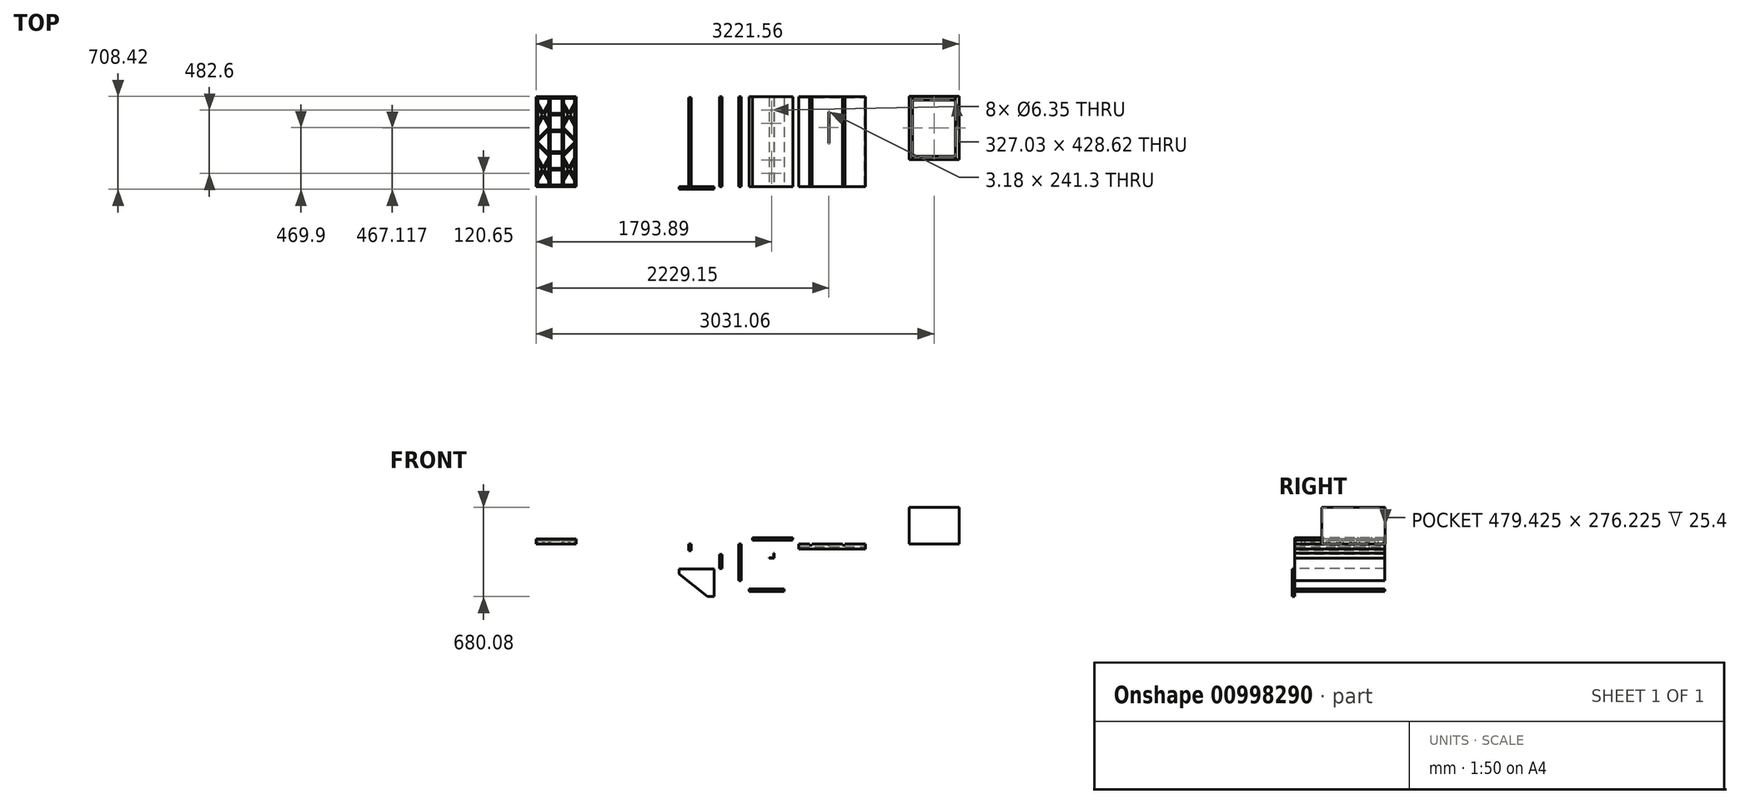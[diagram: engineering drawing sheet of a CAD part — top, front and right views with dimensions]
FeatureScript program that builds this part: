
annotation { "Feature Type Name" : "Feature", "Feature Type Description" : "" }
export const myFeature = defineFeature(function(context is Context, id is Id, definition is map)
    precondition{}
    {
        {
            var Q0;
            Q0=qCreatedBy(makeId("Front.planeOp"),FACE);
            var sketch = newSketch(context, id + "F0", { "sketchPlane" : qUnion([Q0])});
            skLineSegment(sketch, "E0", {"start": v(0, 0) * mm, "end": v(508, 0) * mm});
            skLineSegment(sketch, "E1", {"start": v(508, 0) * mm, "end": v(508, -38.1) * mm});
            skLineSegment(sketch, "E2", {"start": v(508, -38.1) * mm, "end": v(0, -38.1) * mm});
            skLineSegment(sketch, "E3", {"start": v(0, -38.1) * mm, "end": v(0, 0) * mm});
            skSolve(sketch);
        }
        {
            var Q0;
            Q0=makeQuery(id+"F0.imprint","IMPRINT",FACE,{"disambiguationData":[TD([[makeQuery(id+"F0.imprint","IMPRINT",EDGE,{"derivedFrom":sQuery(id+"F0.wireOp",EDGE,"E0")}),-1.0]])]});
            extrude(context, id + "F1", {"entities" : qUnion([Q0]), "oppositeDirection" : true, "depth" : 685.8 * mm, "offsetDistance" : 25.4 * mm});
        }
        {
            var Q0;
            Q0=qCreatedBy(makeId("Front.planeOp"),FACE);
            var sketch = newSketch(context, id + "F2", { "sketchPlane" : qUnion([Q0])});
            skLineSegment(sketch, "E4", {"start": v(-187.6, -68.5) * mm, "end": v(-187.6, -106.6) * mm});
            skLineSegment(sketch, "E5", {"start": v(-187.6, -106.6) * mm, "end": v(-225.7, -106.6) * mm});
            skLineSegment(sketch, "E6", {"start": v(-225.7, -106.6) * mm, "end": v(-225.7, -103.42) * mm});
            skLineSegment(sketch, "E7", {"start": v(-225.7, -103.42) * mm, "end": v(-190.78, -103.42) * mm});
            skLineSegment(sketch, "E8", {"start": v(-190.78, -103.42) * mm, "end": v(-190.78, -68.5) * mm});
            skLineSegment(sketch, "E9", {"start": v(-190.78, -68.5) * mm, "end": v(-187.6, -68.5) * mm});
            skSolve(sketch);
        }
        {
            var Q0;
            Q0=makeQuery(id+"F2.imprint","IMPRINT",FACE,{"disambiguationData":[TD([[makeQuery(id+"F2.imprint","IMPRINT",EDGE,{"derivedFrom":sQuery(id+"F2.wireOp",EDGE,"E4")}),-1.0]])]});
            var Q1;
            Q1=makeQuery(id+"F1.opExtrude","CAP_VERTEX",VERTEX,{"disambiguationData":[OSD([sQuery(id+"F0.wireOp",EDGE,"E0"),sQuery(id+"F0.wireOp",EDGE,"E3")])],"isStart":false});
            extrude(context, id + "F3", {"entities" : qUnion([Q0]), "endBound" : BoundingType.UP_TO_VERTEX, "oppositeDirection" : true, "depth" : 25.4 * mm, "endBoundEntityVertex" : qUnion([Q1]), "offsetDistance" : 25.4 * mm});
        }
        {
            var Q0;
            Q0=qCreatedBy(makeId("Front.planeOp"),FACE);
            var sketch = newSketch(context, id + "F4", { "sketchPlane" : qUnion([Q0])});
            skLineSegment(sketch, "E10.bottom", {"start": v(-351.49, 47.66) * mm, "end": v(-46.69, 47.66) * mm});
            skLineSegment(sketch, "E10.top", {"start": v(-351.49, 28.61) * mm, "end": v(-46.69, 28.61) * mm});
            skLineSegment(sketch, "E10.left", {"start": v(-351.49, 47.66) * mm, "end": v(-351.49, 28.61) * mm});
            skLineSegment(sketch, "E10.right", {"start": v(-46.69, 47.66) * mm, "end": v(-46.69, 28.61) * mm});
            skSolve(sketch);
        }
        {
            var Q0;
            Q0=makeQuery(id+"F4.imprint","IMPRINT",FACE,{"disambiguationData":[TD([[makeQuery(id+"F4.imprint","IMPRINT",EDGE,{"derivedFrom":sQuery(id+"F4.wireOp",EDGE,"E10.bottom")}),-1.0]])]});
            var Q1;
            Q1=makeQuery(id+"F1.opExtrude","CAP_VERTEX",VERTEX,{"disambiguationData":[OSD([sQuery(id+"F0.wireOp",EDGE,"E0"),sQuery(id+"F0.wireOp",EDGE,"E3")])],"isStart":false});
            extrude(context, id + "F5", {"entities" : qUnion([Q0]), "endBound" : BoundingType.UP_TO_VERTEX, "oppositeDirection" : true, "depth" : 25.4 * mm, "endBoundEntityVertex" : qUnion([Q1]), "offsetDistance" : 25.4 * mm});
        }
        {
            var Q0;
            Q0=qCreatedBy(makeId("Front.planeOp"),FACE);
            var sketch = newSketch(context, id + "F6", { "sketchPlane" : qUnion([Q0])});
            skLineSegment(sketch, "E11", {"start": v(-457.67, 0) * mm, "end": v(-438.62, 0) * mm});
            skLineSegment(sketch, "E12", {"start": v(-438.62, -279.4) * mm, "end": v(-457.67, -279.4) * mm});
            skLineSegment(sketch, "E13", {"start": v(-457.67, -279.4) * mm, "end": v(-457.67, 0) * mm});
            skLineSegment(sketch, "E14", {"start": v(-438.62, -279.4) * mm, "end": v(-438.62, 0) * mm});
            skSolve(sketch);
        }
        {
            var Q0;
            Q0=makeQuery(id+"F6.imprint","IMPRINT",FACE,{"disambiguationData":[TD([[makeQuery(id+"F6.imprint","IMPRINT",EDGE,{"derivedFrom":sQuery(id+"F6.wireOp",EDGE,"E11")}),-1.0]])]});
            var Q1;
            Q1=makeQuery(id+"F1.opExtrude","CAP_VERTEX",VERTEX,{"disambiguationData":[OSD([sQuery(id+"F0.wireOp",EDGE,"E0"),sQuery(id+"F0.wireOp",EDGE,"E3")])],"isStart":false});
            extrude(context, id + "F7", {"entities" : qUnion([Q0]), "operationType" : NewBodyOperationType.ADD, "endBound" : BoundingType.UP_TO_VERTEX, "oppositeDirection" : true, "depth" : 25.4 * mm, "endBoundEntityVertex" : qUnion([Q1]), "offsetDistance" : 25.4 * mm});
        }
        {
            var Q0;
            Q0=makeQuery(id+"F1.opExtrude","SWEPT_FACE",FACE,{"disambiguationData":[OSD([sQuery(id+"F0.wireOp",EDGE,"E2")])]});
            var sketch = newSketch(context, id + "F8", { "sketchPlane" : qUnion([Q0])});
            skLineSegment(sketch, "E15.bottom", {"start": v(6.35, -6.35) * mm, "end": v(501.65, -6.35) * mm});
            skLineSegment(sketch, "E15.top", {"start": v(6.35, -679.45) * mm, "end": v(501.65, -679.45) * mm});
            skLineSegment(sketch, "E15.left", {"start": v(6.35, -6.35) * mm, "end": v(6.35, -679.45) * mm});
            skLineSegment(sketch, "E15.right", {"start": v(501.65, -6.35) * mm, "end": v(501.65, -679.45) * mm});
            skSolve(sketch);
        }
        {
            var Q0;
            Q0=makeQuery(id+"F8.imprint","IMPRINT",FACE,{"disambiguationData":[TD([[makeQuery(id+"F8.imprint","IMPRINT",EDGE,{"derivedFrom":sQuery(id+"F8.wireOp",EDGE,"E15.bottom")}),-1.0]])]});
            extrude(context, id + "F9", {"entities" : qUnion([Q0]), "operationType" : NewBodyOperationType.REMOVE, "oppositeDirection" : true, "depth" : 19.05 * mm, "offsetDistance" : 25.4 * mm});
        }
        {
            var Q0;
            Q0=makeQuery(id+"F5.opExtrude","SWEPT_FACE",FACE,{"disambiguationData":[OSD([sQuery(id+"F4.wireOp",EDGE,"E10.right")])]});
            var sketch = newSketch(context, id + "F10", { "sketchPlane" : qUnion([Q0])});
            skLineSegment(sketch, "E16", {"start": v(0, 41.31) * mm, "end": v(685.8, 41.31) * mm});
            skSolve(sketch);
        }
        {
            var Q0;
            {var subQ0=sQuery(id+"F10.wireOp",EDGE,"E16");Q0=makeQuery(id+"F10.imprint","IMPRINT",FACE,{"disambiguationData":[TD([[makeQuery(id+"F10.imprint","IMPRINT",EDGE,{"derivedFrom":subQ0}),1.0]])]});}
            extrude(context, id + "F11", {"entities" : qUnion([Q0]), "operationType" : NewBodyOperationType.ADD, "depth" : 3.17 * mm, "offsetDistance" : 25.4 * mm});
        }
        {
            var Q0;
            Q0=makeQuery(id+"F3.opExtrude","SWEPT_FACE",FACE,{"disambiguationData":[OSD([sQuery(id+"F2.wireOp",EDGE,"E5")])]});
            var sketch = newSketch(context, id + "F12", { "sketchPlane" : qUnion([Q0])});
            skCircle(sketch, "E17", {"center": v(-206.66, -101.6) * mm, "radius": 3.18 * mm});
            skPoint(sketch, "E17.centerSnap0", {"position": v(-206.66, 0) * mm});
            skCircle(sketch, "E18", {"center": v(-206.66, -203.2) * mm, "radius": 3.18 * mm});
            skCircle(sketch, "E19", {"center": v(-206.66, -482.6) * mm, "radius": 3.18 * mm});
            skCircle(sketch, "E20", {"center": v(-206.66, -584.2) * mm, "radius": 3.18 * mm});
            skLineSegment(sketch, "E21", {"start": v(-206.66, 0) * mm, "end": v(-206.66, -685.8) * mm, "construction": true});
            skSolve(sketch);
        }
        {
            var Q0;
            Q0 = qSketchRegion(id + "F12", true);
            extrude(context, id + "F13", {"entities" : qUnion([Q0]), "operationType" : NewBodyOperationType.REMOVE, "endBound" : BoundingType.THROUGH_ALL, "oppositeDirection" : true, "depth" : 25.4 * mm, "offsetDistance" : 25.4 * mm});
        }
        {
            var Q0;
            Q0=qCreatedBy(makeId("Front.planeOp"),FACE);
            var sketch = newSketch(context, id + "F14", { "sketchPlane" : qUnion([Q0])});
            skLineSegment(sketch, "E22.bottom", {"start": v(-377.25, -343.66) * mm, "end": v(-110.55, -343.66) * mm});
            skLineSegment(sketch, "E22.top", {"start": v(-377.25, -362.7) * mm, "end": v(-110.55, -362.7) * mm});
            skLineSegment(sketch, "E22.left", {"start": v(-377.25, -343.66) * mm, "end": v(-377.25, -362.7) * mm});
            skLineSegment(sketch, "E22.right", {"start": v(-110.55, -343.66) * mm, "end": v(-110.55, -362.7) * mm});
            skSolve(sketch);
        }
        {
            var Q0;
            Q0 = qSketchRegion(id + "F14", true);
            var Q1;
            Q1=makeQuery(id+"F1.opExtrude","CAP_VERTEX",VERTEX,{"disambiguationData":[OSD([sQuery(id+"F0.wireOp",EDGE,"E0"),sQuery(id+"F0.wireOp",EDGE,"E3")])],"isStart":false});
            extrude(context, id + "F15", {"entities" : qUnion([Q0]), "endBound" : BoundingType.UP_TO_VERTEX, "oppositeDirection" : true, "depth" : 25.4 * mm, "endBoundEntityVertex" : qUnion([Q1]), "offsetDistance" : 25.4 * mm});
        }
        {
            var Q0;
            Q0=qCreatedBy(makeId("Front.planeOp"),FACE);
            var sketch = newSketch(context, id + "F16", { "sketchPlane" : qUnion([Q0])});
            skLineSegment(sketch, "E23.bottom", {"start": v(-839.36, 0) * mm, "end": v(-820.3, 0) * mm});
            skLineSegment(sketch, "E23.top", {"start": v(-839.36, -50.8) * mm, "end": v(-820.3, -50.8) * mm});
            skLineSegment(sketch, "E23.left", {"start": v(-839.36, 0) * mm, "end": v(-839.36, -50.8) * mm});
            skLineSegment(sketch, "E23.right", {"start": v(-820.3, 0) * mm, "end": v(-820.3, -50.8) * mm});
            skSolve(sketch);
        }
        {
            var Q0;
            Q0 = qSketchRegion(id + "F16", true);
            var Q1;
            Q1=makeQuery(id+"F9.boolean.opBoolean","COPY",VERTEX,{"derivedFrom":makeQuery(id+"F9.opExtrude","CAP_VERTEX",VERTEX,{"disambiguationData":[OSD([sQuery(id+"F8.wireOp",EDGE,"E15.top"),sQuery(id+"F8.wireOp",EDGE,"E15.left")])],"isStart":false})});
            extrude(context, id + "F17", {"entities" : qUnion([Q0]), "endBound" : BoundingType.UP_TO_VERTEX, "oppositeDirection" : true, "depth" : 25.4 * mm, "endBoundEntityVertex" : qUnion([Q1]), "offsetDistance" : 25.4 * mm});
        }
        {
            var Q0;
            Q0=qCreatedBy(makeId("Front.planeOp"),FACE);
            var sketch = newSketch(context, id + "F18", { "sketchPlane" : qUnion([Q0])});
            skLineSegment(sketch, "E24.bottom", {"start": v(-602.45, -79.5) * mm, "end": v(-583.4, -79.5) * mm});
            skLineSegment(sketch, "E24.top", {"start": v(-602.45, -187.44) * mm, "end": v(-583.4, -187.44) * mm});
            skLineSegment(sketch, "E24.left", {"start": v(-602.45, -79.5) * mm, "end": v(-602.45, -187.44) * mm});
            skLineSegment(sketch, "E24.right", {"start": v(-583.4, -79.5) * mm, "end": v(-583.4, -187.44) * mm});
            skSolve(sketch);
        }
        {
            var Q0;
            Q0 = qSketchRegion(id + "F18", true);
            var Q1;
            Q1=makeQuery(id+"F1.opExtrude","CAP_VERTEX",VERTEX,{"disambiguationData":[OSD([sQuery(id+"F0.wireOp",EDGE,"E0"),sQuery(id+"F0.wireOp",EDGE,"E3")])],"isStart":false});
            extrude(context, id + "F19", {"entities" : qUnion([Q0]), "endBound" : BoundingType.UP_TO_VERTEX, "oppositeDirection" : true, "depth" : 25.4 * mm, "endBoundEntityVertex" : qUnion([Q1]), "offsetDistance" : 25.4 * mm});
        }
        {
            var Q0;
            Q0=qCreatedBy(makeId("Front.planeOp"),FACE);
            var sketch = newSketch(context, id + "F20", { "sketchPlane" : qUnion([Q0])});
            skLineSegment(sketch, "E25", {"start": v(-912.68, -191.13) * mm, "end": v(-645.98, -191.13) * mm});
            skLineSegment(sketch, "E26", {"start": v(-645.98, -191.13) * mm, "end": v(-645.98, -400.68) * mm});
            skLineSegment(sketch, "E27", {"start": v(-912.68, -191.13) * mm, "end": v(-912.68, -229.23) * mm});
            skLineSegment(sketch, "E28", {"start": v(-645.98, -400.68) * mm, "end": v(-696.78, -400.68) * mm});
            skLineSegment(sketch, "E29", {"start": v(-696.78, -400.68) * mm, "end": v(-912.68, -229.23) * mm});
            skSolve(sketch);
        }
        {
            var Q0;
            Q0 = qSketchRegion(id + "F20", true);
            extrude(context, id + "F21", {"entities" : qUnion([Q0]), "depth" : 19.05 * mm, "offsetDistance" : 25.4 * mm});
        }
        {
            var Q0;
            Q0=makeQuery(id+"F1.opExtrude","CAP_FACE",FACE,{"disambiguationData":[OSD([sQuery(id+"F0.wireOp",EDGE,"E0"),sQuery(id+"F0.wireOp",EDGE,"E1"),sQuery(id+"F0.wireOp",EDGE,"EEyE07IA-I6JG-BArI-9bJA-Gx0k7tiSzJfB"),sQuery(id+"F0.wireOp",EDGE,"jnxuvKVA-eAux-85X3-3hQU-5fmw7PvYRqck"),sQuery(id+"F0.wireOp",EDGE,"E2"),sQuery(id+"F0.wireOp",EDGE,"E3")])],"isStart":true});
            var sketch = newSketch(context, id + "F22", { "sketchPlane" : qUnion([Q0])});
            skLineSegment(sketch, "E30.bottom", {"start": v(80.96, 0) * mm, "end": v(100.01, 0) * mm});
            skLineSegment(sketch, "E30.top", {"start": v(80.96, -9.53) * mm, "end": v(100.01, -9.53) * mm});
            skLineSegment(sketch, "E30.left", {"start": v(80.96, 0) * mm, "end": v(80.96, -9.53) * mm});
            skLineSegment(sketch, "E30.right", {"start": v(100.01, 0) * mm, "end": v(100.01, -9.53) * mm});
            skLineSegment(sketch, "E31.bottom", {"start": v(331.79, 0) * mm, "end": v(350.84, 0) * mm});
            skLineSegment(sketch, "E31.top", {"start": v(331.79, -9.52) * mm, "end": v(350.84, -9.52) * mm});
            skLineSegment(sketch, "E31.left", {"start": v(331.79, 0) * mm, "end": v(331.79, -9.52) * mm});
            skLineSegment(sketch, "E31.right", {"start": v(350.84, 0) * mm, "end": v(350.84, -9.52) * mm});
            skSolve(sketch);
        }
        {
            var Q0;
            Q0 = qSketchRegion(id + "F22", true);
            extrude(context, id + "F23", {"entities" : qUnion([Q0]), "operationType" : NewBodyOperationType.REMOVE, "endBound" : BoundingType.THROUGH_ALL, "oppositeDirection" : true, "depth" : 25.4 * mm, "offsetDistance" : 25.4 * mm});
        }
        {
            var Q0;
            {var subQ5=sQuery(id+"F0.wireOp",EDGE,"E0");Q0=makeQuery(id+"F23.boolean.opBoolean","SPLIT",FACE,{"disambiguationData":[TD([makeQuery(id+"F23.opExtrude","SWEPT_FACE",FACE,{"disambiguationData":[OSD([sQuery(id+"F22.wireOp",EDGE,"E30.right")])]})])],"derivedFrom":makeQuery(id+"F1.opExtrude","SWEPT_FACE",FACE,{"disambiguationData":[OSD([subQ5])]})});}
            var sketch = newSketch(context, id + "F24", { "sketchPlane" : qUnion([Q0])});
            skLineSegment(sketch, "E32.bottom", {"start": v(227.01, 571.5) * mm, "end": v(230.19, 571.5) * mm});
            skLineSegment(sketch, "E32.top", {"start": v(227.01, 330.2) * mm, "end": v(230.19, 330.2) * mm});
            skLineSegment(sketch, "E32.left", {"start": v(227.01, 571.5) * mm, "end": v(227.01, 330.2) * mm});
            skLineSegment(sketch, "E32.right", {"start": v(230.19, 571.5) * mm, "end": v(230.19, 330.2) * mm});
            skSolve(sketch);
        }
        {
            var Q0;
            Q0 = qSketchRegion(id + "F24", true);
            extrude(context, id + "F25", {"entities" : qUnion([Q0]), "operationType" : NewBodyOperationType.REMOVE, "endBound" : BoundingType.THROUGH_ALL, "oppositeDirection" : true, "depth" : 25.4 * mm, "offsetDistance" : 25.4 * mm});
        }
        {
            var Q0;
            Q0=qCreatedBy(makeId("Top.planeOp"),FACE);
            var sketch = newSketch(context, id + "F26", { "sketchPlane" : qUnion([Q0])});
            skLineSegment(sketch, "E33.bottom", {"start": v(840.01, 689.37) * mm, "end": v(1221.01, 689.37) * mm});
            skLineSegment(sketch, "E33.top", {"start": v(840.01, 206.77) * mm, "end": v(1221.01, 206.77) * mm});
            skLineSegment(sketch, "E33.left", {"start": v(840.01, 689.37) * mm, "end": v(840.01, 206.77) * mm});
            skLineSegment(sketch, "E33.right", {"start": v(1221.01, 689.37) * mm, "end": v(1221.01, 206.77) * mm});
            skSolve(sketch);
        }
        {
            var Q0;
            Q0 = qSketchRegion(id + "F26", true);
            extrude(context, id + "F27", {"entities" : qUnion([Q0]), "depth" : 279.4 * mm, "offsetDistance" : 25.4 * mm});
        }
        {
            var Q0;
            Q0=makeQuery(id+"F27.opExtrude","CAP_FACE",FACE,{"disambiguationData":[OSD([sQuery(id+"F26.wireOp",EDGE,"E33.bottom"),sQuery(id+"F26.wireOp",EDGE,"E33.top"),sQuery(id+"F26.wireOp",EDGE,"E33.left"),sQuery(id+"F26.wireOp",EDGE,"E33.right")])],"isStart":false});
            var sketch = newSketch(context, id + "F28", { "sketchPlane" : qUnion([Q0])});
            skLineSegment(sketch, "E34.bottom", {"start": v(867, 662.38) * mm, "end": v(1194.03, 662.38) * mm});
            skLineSegment(sketch, "E34.top", {"start": v(867, 233.75) * mm, "end": v(1194.03, 233.75) * mm});
            skLineSegment(sketch, "E34.left", {"start": v(867, 662.38) * mm, "end": v(867, 233.75) * mm});
            skLineSegment(sketch, "E34.right", {"start": v(1194.03, 662.38) * mm, "end": v(1194.03, 233.75) * mm});
            skSolve(sketch);
        }
        {
            var Q0;
            Q0 = qSketchRegion(id + "F28", true);
            extrude(context, id + "F29", {"entities" : qUnion([Q0]), "operationType" : NewBodyOperationType.REMOVE, "endBound" : BoundingType.THROUGH_ALL, "oppositeDirection" : true, "depth" : 25.4 * mm, "offsetDistance" : 25.4 * mm});
        }
        {
            var Q0;
            Q0=makeQuery(id+"F29.boolean.opBoolean","COPY",FACE,{"derivedFrom":makeQuery(id+"F29.opExtrude","SWEPT_FACE",FACE,{"disambiguationData":[OSD([sQuery(id+"F28.wireOp",EDGE,"E34.left")])]})});
            var sketch = newSketch(context, id + "F30", { "sketchPlane" : qUnion([Q0])});
            skLineSegment(sketch, "E35.bottom", {"start": v(233.75, 277.81) * mm, "end": v(662.38, 277.81) * mm});
            skLineSegment(sketch, "E35.top", {"start": v(233.75, 1.59) * mm, "end": v(662.38, 1.59) * mm});
            skLineSegment(sketch, "E35.left", {"start": v(233.75, 277.81) * mm, "end": v(233.75, 1.59) * mm});
            skLineSegment(sketch, "E35.right", {"start": v(662.38, 277.81) * mm, "end": v(662.38, 1.59) * mm});
            skSolve(sketch);
        }
        {
            var Q0;
            Q0 = qSketchRegion(id + "F30", true);
            extrude(context, id + "F31", {"entities" : qUnion([Q0]), "operationType" : NewBodyOperationType.REMOVE, "oppositeDirection" : true, "depth" : 25.4 * mm, "offsetDistance" : 25.4 * mm});
        }
        {
            var Q0;
            Q0=makeQuery(id+"F29.boolean.opBoolean","COPY",FACE,{"derivedFrom":makeQuery(id+"F29.opExtrude","SWEPT_FACE",FACE,{"disambiguationData":[OSD([sQuery(id+"F28.wireOp",EDGE,"E34.right")])]})});
            var sketch = newSketch(context, id + "F32", { "sketchPlane" : qUnion([Q0])});
            skLineSegment(sketch, "E36.bottom", {"start": v(-662.38, 277.81) * mm, "end": v(-233.75, 277.81) * mm});
            skLineSegment(sketch, "E36.top", {"start": v(-662.38, 1.59) * mm, "end": v(-233.75, 1.59) * mm});
            skLineSegment(sketch, "E36.left", {"start": v(-662.38, 277.81) * mm, "end": v(-662.38, 1.59) * mm});
            skLineSegment(sketch, "E36.right", {"start": v(-233.75, 277.81) * mm, "end": v(-233.75, 1.59) * mm});
            skSolve(sketch);
        }
        {
            var Q0;
            Q0 = qSketchRegion(id + "F32", true);
            extrude(context, id + "F33", {"entities" : qUnion([Q0]), "operationType" : NewBodyOperationType.REMOVE, "oppositeDirection" : true, "depth" : 25.4 * mm, "offsetDistance" : 25.4 * mm});
        }
        {
            var Q0;
            Q0=makeQuery(id+"F33.boolean.opBoolean","MERGE",FACE,{"derivedFrom":[makeQuery(id+"F31.boolean.opBoolean","MERGE",FACE,{"derivedFrom":[makeQuery(id+"F29.boolean.opBoolean","COPY",FACE,{"derivedFrom":makeQuery(id+"F29.opExtrude","SWEPT_FACE",FACE,{"disambiguationData":[OSD([sQuery(id+"F28.wireOp",EDGE,"E34.bottom")])]})})],"fromTools":[makeQuery(id+"F31.opExtrude","SWEPT_FACE",FACE,{"disambiguationData":[OSD([sQuery(id+"F30.wireOp",EDGE,"E35.right")])]})]})],"fromTools":[makeQuery(id+"F33.opExtrude","SWEPT_FACE",FACE,{"disambiguationData":[OSD([sQuery(id+"F32.wireOp",EDGE,"E36.left")])]})]});
            var sketch = newSketch(context, id + "F34", { "sketchPlane" : qUnion([Q0])});
            skLineSegment(sketch, "E37", {"start": v(867, 279.4) * mm, "end": v(867, 277.81) * mm});
            skLineSegment(sketch, "E38", {"start": v(867, 277.81) * mm, "end": v(841.6, 277.81) * mm});
            skLineSegment(sketch, "E39", {"start": v(841.6, 277.81) * mm, "end": v(841.6, 1.59) * mm});
            skLineSegment(sketch, "E40", {"start": v(841.6, 1.59) * mm, "end": v(1219.43, 1.59) * mm});
            skLineSegment(sketch, "E41", {"start": v(1219.43, 1.59) * mm, "end": v(1219.43, 277.81) * mm});
            skLineSegment(sketch, "E42", {"start": v(1219.43, 277.81) * mm, "end": v(1194.03, 277.81) * mm});
            skLineSegment(sketch, "E43", {"start": v(1194.03, 277.81) * mm, "end": v(1194.03, 279.4) * mm});
            skLineSegment(sketch, "E44", {"start": v(1194.03, 279.4) * mm, "end": v(867, 279.4) * mm});
            skSolve(sketch);
        }
        {
            var Q0;
            Q0 = qSketchRegion(id + "F34", true);
            extrude(context, id + "F35", {"entities" : qUnion([Q0]), "operationType" : NewBodyOperationType.REMOVE, "oppositeDirection" : true, "depth" : 25.4 * mm, "offsetDistance" : 25.4 * mm});
        }
        {
            var Q0;
            Q0=makeQuery(id+"F33.boolean.opBoolean","MERGE",FACE,{"derivedFrom":[makeQuery(id+"F31.boolean.opBoolean","MERGE",FACE,{"derivedFrom":[makeQuery(id+"F29.boolean.opBoolean","COPY",FACE,{"derivedFrom":makeQuery(id+"F29.opExtrude","SWEPT_FACE",FACE,{"disambiguationData":[OSD([sQuery(id+"F28.wireOp",EDGE,"E34.top")])]})})],"fromTools":[makeQuery(id+"F31.opExtrude","SWEPT_FACE",FACE,{"disambiguationData":[OSD([sQuery(id+"F30.wireOp",EDGE,"E35.left")])]})]})],"fromTools":[makeQuery(id+"F33.opExtrude","SWEPT_FACE",FACE,{"disambiguationData":[OSD([sQuery(id+"F32.wireOp",EDGE,"E36.right")])]})]});
            var sketch = newSketch(context, id + "F36", { "sketchPlane" : qUnion([Q0])});
            skLineSegment(sketch, "E45", {"start": v(-867, 279.4) * mm, "end": v(-1194.03, 279.4) * mm});
            skLineSegment(sketch, "E46", {"start": v(-1194.03, 279.4) * mm, "end": v(-1194.03, 277.81) * mm});
            skLineSegment(sketch, "E47", {"start": v(-1194.03, 277.81) * mm, "end": v(-1219.43, 277.81) * mm});
            skLineSegment(sketch, "E48", {"start": v(-1219.43, 277.81) * mm, "end": v(-1219.43, 1.59) * mm});
            skLineSegment(sketch, "E49", {"start": v(-1219.43, 1.59) * mm, "end": v(-841.6, 1.59) * mm});
            skLineSegment(sketch, "E50", {"start": v(-867, 277.81) * mm, "end": v(-867, 277.81) * mm});
            skLineSegment(sketch, "E51", {"start": v(-867, 277.81) * mm, "end": v(-867, 279.4) * mm});
            skLineSegment(sketch, "E52", {"start": v(-867, 277.81) * mm, "end": v(-841.6, 277.81) * mm});
            skLineSegment(sketch, "E53", {"start": v(-841.6, 277.81) * mm, "end": v(-841.6, 1.59) * mm});
            skSolve(sketch);
        }
        {
            var Q0;
            Q0 = qSketchRegion(id + "F36", true);
            extrude(context, id + "F37", {"entities" : qUnion([Q0]), "operationType" : NewBodyOperationType.REMOVE, "oppositeDirection" : true, "depth" : 25.4 * mm, "offsetDistance" : 25.4 * mm});
        }
        {
            var Q0;
            Q0=qCreatedBy(makeId("Top.planeOp"),FACE);
            var sketch = newSketch(context, id + "F38", { "sketchPlane" : qUnion([Q0])});
            skLineSegment(sketch, "E54.bottom", {"start": v(-2000.55, 685.8) * mm, "end": v(-1695.75, 685.8) * mm});
            skLineSegment(sketch, "E54.top", {"start": v(-2000.55, 0) * mm, "end": v(-1695.75, 0) * mm});
            skLineSegment(sketch, "E54.left", {"start": v(-2000.55, 685.8) * mm, "end": v(-2000.55, 0) * mm});
            skLineSegment(sketch, "E54.right", {"start": v(-1695.75, 685.8) * mm, "end": v(-1695.75, 0) * mm});
            skSolve(sketch);
        }
        {
            var Q0;
            Q0 = qSketchRegion(id + "F38", true);
            extrude(context, id + "F39", {"entities" : qUnion([Q0]), "depth" : 38.1 * mm, "offsetDistance" : 25.4 * mm});
        }
        {
            var Q0;
            Q0=makeQuery(id+"F39.opExtrude","CAP_FACE",FACE,{"disambiguationData":[OSD([sQuery(id+"F38.wireOp",EDGE,"E54.bottom"),sQuery(id+"F38.wireOp",EDGE,"E54.top"),sQuery(id+"F38.wireOp",EDGE,"E54.left"),sQuery(id+"F38.wireOp",EDGE,"E54.right")])],"isStart":false});
            var sketch = newSketch(context, id + "F40", { "sketchPlane" : qUnion([Q0])});
            skLineSegment(sketch, "E55", {"start": v(-1898.95, 685.8) * mm, "end": v(-1898.95, 0) * mm, "construction": true});
            skLineSegment(sketch, "E56", {"start": v(-1797.35, 685.8) * mm, "end": v(-1797.35, 0) * mm, "construction": true});
            skLineSegment(sketch, "E57.bottom", {"start": v(-1987.85, 673.1) * mm, "end": v(-1905.3, 673.1) * mm});
            skLineSegment(sketch, "E57.top", {"start": v(-1987.85, 12.7) * mm, "end": v(-1905.3, 12.7) * mm});
            skLineSegment(sketch, "E58.bottom", {"start": v(-1892.6, 673.1) * mm, "end": v(-1803.7, 673.1) * mm});
            skLineSegment(sketch, "E58.top", {"start": v(-1892.6, 12.7) * mm, "end": v(-1803.7, 12.7) * mm});
            skLineSegment(sketch, "E58.left", {"start": v(-1892.6, 673.1) * mm, "end": v(-1892.6, 12.7) * mm});
            skLineSegment(sketch, "E58.right", {"start": v(-1803.7, 673.1) * mm, "end": v(-1803.7, 12.7) * mm});
            skLineSegment(sketch, "E59.bottom", {"start": v(-1791, 673.1) * mm, "end": v(-1708.45, 673.1) * mm});
            skLineSegment(sketch, "E59.top", {"start": v(-1791, 12.7) * mm, "end": v(-1708.45, 12.7) * mm});
            skLineSegment(sketch, "E59.left", {"start": v(-1791, 673.1) * mm, "end": v(-1791, 12.7) * mm});
            skLineSegment(sketch, "E59.right", {"start": v(-1708.45, 673.1) * mm, "end": v(-1708.45, 12.7) * mm});
            skLineSegment(sketch, "E60", {"start": v(-1987.85, 673.1) * mm, "end": v(-1987.85, 12.7) * mm});
            skLineSegment(sketch, "E61", {"start": v(-1905.3, 12.7) * mm, "end": v(-1905.3, 673.1) * mm});
            skSolve(sketch);
        }
        {
            var Q0;
            Q0 = qSketchRegion(id + "F40", true);
            extrude(context, id + "F41", {"entities" : qUnion([Q0]), "operationType" : NewBodyOperationType.REMOVE, "endBound" : BoundingType.THROUGH_ALL, "oppositeDirection" : true, "depth" : 25.4 * mm, "offsetDistance" : 25.4 * mm});
        }
        {
            var Q0;
            Q0=makeQuery(id+"F39.opExtrude","CAP_FACE",FACE,{"disambiguationData":[OSD([sQuery(id+"F38.wireOp",EDGE,"E54.bottom"),sQuery(id+"F38.wireOp",EDGE,"E54.top"),sQuery(id+"F38.wireOp",EDGE,"E54.left"),sQuery(id+"F38.wireOp",EDGE,"E54.right")])],"isStart":false});
            var sketch = newSketch(context, id + "F42", { "sketchPlane" : qUnion([Q0])});
            skLineSegment(sketch, "E62.bottom", {"start": v(-1987.85, 673.1) * mm, "end": v(-1987.85, 673.1) * mm});
            skLineSegment(sketch, "E62.top", {"start": v(-1987.85, 12.7) * mm, "end": v(-1987.85, 12.7) * mm});
            skLineSegment(sketch, "E62.left", {"start": v(-1987.85, 673.1) * mm, "end": v(-1987.85, 12.7) * mm});
            skLineSegment(sketch, "E62.right", {"start": v(-1987.85, 673.1) * mm, "end": v(-1987.85, 12.7) * mm});
            skLineSegment(sketch, "E63.bottom", {"start": v(-1892.6, 673.1) * mm, "end": v(-1803.7, 673.1) * mm});
            skLineSegment(sketch, "E63.top", {"start": v(-1892.6, 12.7) * mm, "end": v(-1803.7, 12.7) * mm});
            skLineSegment(sketch, "E63.left", {"start": v(-1892.6, 673.1) * mm, "end": v(-1892.6, 12.7) * mm});
            skLineSegment(sketch, "E63.right", {"start": v(-1803.7, 673.1) * mm, "end": v(-1803.7, 12.7) * mm});
            skLineSegment(sketch, "E64.bottom", {"start": v(-1791, 673.1) * mm, "end": v(-1708.45, 673.1) * mm});
            skLineSegment(sketch, "E64.top", {"start": v(-1791, 12.7) * mm, "end": v(-1708.45, 12.7) * mm});
            skLineSegment(sketch, "E64.left", {"start": v(-1791, 673.1) * mm, "end": v(-1791, 12.7) * mm});
            skLineSegment(sketch, "E64.right", {"start": v(-1708.45, 673.1) * mm, "end": v(-1708.45, 12.7) * mm});
            skSolve(sketch);
        }
        {
            var Q0;
            Q0 = qSketchRegion(id + "F42", true);
            extrude(context, id + "F43", {"entities" : qUnion([Q0]), "operationType" : NewBodyOperationType.REMOVE, "oppositeDirection" : true, "depth" : 6.35 * mm, "offsetDistance" : 25.4 * mm});
        }
        {
            var Q0;
            Q0=makeQuery(id+"F39.opExtrude","CAP_FACE",FACE,{"disambiguationData":[OSD([sQuery(id+"F38.wireOp",EDGE,"E54.bottom"),sQuery(id+"F38.wireOp",EDGE,"E54.top"),sQuery(id+"F38.wireOp",EDGE,"E54.left"),sQuery(id+"F38.wireOp",EDGE,"E54.right")])],"isStart":true});
            var sketch = newSketch(context, id + "F44", { "sketchPlane" : qUnion([Q0])});
            skLineSegment(sketch, "E65", {"start": v(-1791, -50.8) * mm, "end": v(-1791, -76.2) * mm});
            skLineSegment(sketch, "E66", {"start": v(-1791, -76.2) * mm, "end": v(-1757.06, -135) * mm});
            skLineSegment(sketch, "E67", {"start": v(-1757.06, -135) * mm, "end": v(-1791, -193.78) * mm});
            skLineSegment(sketch, "E68", {"start": v(-1791, -193.78) * mm, "end": v(-1791, -219.18) * mm});
            skLineSegment(sketch, "E69", {"start": v(-1791, -219.18) * mm, "end": v(-1749.73, -147.7) * mm});
            skLineSegment(sketch, "E70", {"start": v(-1749.73, -147.7) * mm, "end": v(-1708.45, -219.18) * mm});
            skLineSegment(sketch, "E71", {"start": v(-1708.45, -219.18) * mm, "end": v(-1708.45, -193.78) * mm});
            skLineSegment(sketch, "E72", {"start": v(-1708.45, -193.78) * mm, "end": v(-1742.4, -135) * mm});
            skLineSegment(sketch, "E73", {"start": v(-1742.4, -135) * mm, "end": v(-1708.45, -76.2) * mm});
            skLineSegment(sketch, "E74", {"start": v(-1708.45, -76.2) * mm, "end": v(-1708.45, -50.8) * mm});
            skLineSegment(sketch, "E75", {"start": v(-1708.45, -50.8) * mm, "end": v(-1749.73, -122.3) * mm});
            skLineSegment(sketch, "E76", {"start": v(-1749.73, -122.3) * mm, "end": v(-1791, -50.8) * mm});
            skLineSegment(sketch, "E77", {"start": v(-1749.73, 84.59) * mm, "end": v(-1749.73, -834.7) * mm, "construction": true});
            skPoint(sketch, "E77.startSnap0", {"position": v(-1749.73, -12.7) * mm});
            skLineSegment(sketch, "E78", {"start": v(-1791, -466.62) * mm, "end": v(-1791, -492.02) * mm});
            skLineSegment(sketch, "E79", {"start": v(-1791, -492.02) * mm, "end": v(-1757.06, -550.8) * mm});
            skLineSegment(sketch, "E80", {"start": v(-1757.06, -550.8) * mm, "end": v(-1791, -609.6) * mm});
            skLineSegment(sketch, "E81", {"start": v(-1791, -609.6) * mm, "end": v(-1791, -635) * mm});
            skLineSegment(sketch, "E82", {"start": v(-1791, -635) * mm, "end": v(-1749.73, -563.5) * mm});
            skLineSegment(sketch, "E83", {"start": v(-1749.73, -563.5) * mm, "end": v(-1708.45, -635) * mm});
            skLineSegment(sketch, "E84", {"start": v(-1708.45, -635) * mm, "end": v(-1708.45, -609.6) * mm});
            skLineSegment(sketch, "E85", {"start": v(-1708.45, -609.6) * mm, "end": v(-1742.4, -550.8) * mm});
            skLineSegment(sketch, "E86", {"start": v(-1742.4, -550.8) * mm, "end": v(-1708.45, -492.02) * mm});
            skLineSegment(sketch, "E87", {"start": v(-1708.45, -492.02) * mm, "end": v(-1708.45, -466.62) * mm});
            skLineSegment(sketch, "E88", {"start": v(-1708.45, -466.62) * mm, "end": v(-1749.73, -538.1) * mm});
            skLineSegment(sketch, "E89", {"start": v(-1749.73, -538.1) * mm, "end": v(-1791, -466.62) * mm});
            skPoint(sketch, "E90.startSnap0", {"position": v(-1753.57, -381) * mm});
            skLineSegment(sketch, "E91", {"start": v(-1708.45, -349.25) * mm, "end": v(-1791, -431.8) * mm});
            skLineSegment(sketch, "E92", {"start": v(-1791, -449.76) * mm, "end": v(-1791, -431.8) * mm});
            skLineSegment(sketch, "E93", {"start": v(-1791, -449.76) * mm, "end": v(-1708.45, -367.21) * mm});
            skLineSegment(sketch, "E94", {"start": v(-1708.45, -349.25) * mm, "end": v(-1708.45, -367.21) * mm});
            skLineSegment(sketch, "E95", {"start": v(-2095.54, -342.9) * mm, "end": v(-1456.93, -342.9) * mm, "construction": true});
            skLineSegment(sketch, "E96", {"start": v(-1708.45, -336.55) * mm, "end": v(-1791, -254) * mm});
            skLineSegment(sketch, "E97", {"start": v(-1791, -254) * mm, "end": v(-1791, -236.04) * mm});
            skLineSegment(sketch, "E98", {"start": v(-1791, -236.04) * mm, "end": v(-1708.45, -318.59) * mm});
            skLineSegment(sketch, "E99", {"start": v(-1708.45, -318.59) * mm, "end": v(-1708.45, -336.55) * mm});
            skLineSegment(sketch, "E100", {"start": v(-1848.15, 88.4) * mm, "end": v(-1848.15, -925.08) * mm, "construction": true});
            skLineSegment(sketch, "E101", {"start": v(-1987.85, -50.8) * mm, "end": v(-1987.85, -76.2) * mm});
            skLineSegment(sketch, "E102", {"start": v(-1987.85, -76.2) * mm, "end": v(-1953.9, -135) * mm});
            skLineSegment(sketch, "E103", {"start": v(-1953.9, -135) * mm, "end": v(-1987.85, -193.78) * mm});
            skLineSegment(sketch, "E104", {"start": v(-1987.85, -193.78) * mm, "end": v(-1987.85, -219.18) * mm});
            skLineSegment(sketch, "E105", {"start": v(-1987.85, -219.18) * mm, "end": v(-1946.58, -147.7) * mm});
            skLineSegment(sketch, "E106", {"start": v(-1946.58, -147.7) * mm, "end": v(-1905.3, -219.18) * mm});
            skLineSegment(sketch, "E107", {"start": v(-1905.3, -219.18) * mm, "end": v(-1905.3, -193.78) * mm});
            skLineSegment(sketch, "E108", {"start": v(-1905.3, -193.78) * mm, "end": v(-1939.24, -135) * mm});
            skLineSegment(sketch, "E109", {"start": v(-1939.24, -135) * mm, "end": v(-1905.3, -76.2) * mm});
            skLineSegment(sketch, "E110", {"start": v(-1905.3, -76.2) * mm, "end": v(-1905.3, -50.8) * mm});
            skLineSegment(sketch, "E111", {"start": v(-1905.3, -50.8) * mm, "end": v(-1946.58, -122.3) * mm});
            skLineSegment(sketch, "E112", {"start": v(-1946.58, -122.3) * mm, "end": v(-1987.85, -50.8) * mm});
            skPoint(sketch, "E113.startSnap0", {"position": v(-1963.47, -26.45) * mm});
            skLineSegment(sketch, "E114", {"start": v(-1987.85, -466.62) * mm, "end": v(-1987.85, -492.02) * mm});
            skLineSegment(sketch, "E115", {"start": v(-1987.85, -492.02) * mm, "end": v(-1953.9, -550.8) * mm});
            skLineSegment(sketch, "E116", {"start": v(-1953.9, -550.8) * mm, "end": v(-1987.85, -609.6) * mm});
            skLineSegment(sketch, "E117", {"start": v(-1987.85, -609.6) * mm, "end": v(-1987.85, -635) * mm});
            skLineSegment(sketch, "E118", {"start": v(-1987.85, -635) * mm, "end": v(-1946.58, -563.5) * mm});
            skLineSegment(sketch, "E119", {"start": v(-1946.58, -563.5) * mm, "end": v(-1905.3, -635) * mm});
            skLineSegment(sketch, "E120", {"start": v(-1905.3, -635) * mm, "end": v(-1905.3, -609.6) * mm});
            skLineSegment(sketch, "E121", {"start": v(-1905.3, -609.6) * mm, "end": v(-1939.24, -550.8) * mm});
            skLineSegment(sketch, "E122", {"start": v(-1939.24, -550.8) * mm, "end": v(-1905.3, -492.02) * mm});
            skLineSegment(sketch, "E123", {"start": v(-1905.3, -492.02) * mm, "end": v(-1905.3, -466.62) * mm});
            skLineSegment(sketch, "E124", {"start": v(-1905.3, -466.62) * mm, "end": v(-1946.58, -538.1) * mm});
            skLineSegment(sketch, "E125", {"start": v(-1946.58, -538.1) * mm, "end": v(-1987.85, -466.62) * mm});
            skPoint(sketch, "E126.startSnap0", {"position": v(-1967.32, -394.74) * mm});
            skLineSegment(sketch, "E127", {"start": v(-1905.3, -431.8) * mm, "end": v(-1987.85, -349.25) * mm});
            skLineSegment(sketch, "E128", {"start": v(-1987.85, -367.21) * mm, "end": v(-1987.85, -349.25) * mm});
            skLineSegment(sketch, "E129", {"start": v(-1987.85, -367.21) * mm, "end": v(-1905.3, -449.76) * mm});
            skLineSegment(sketch, "E130", {"start": v(-1905.3, -431.8) * mm, "end": v(-1905.3, -449.76) * mm});
            skLineSegment(sketch, "E131", {"start": v(-1905.3, -254) * mm, "end": v(-1987.85, -336.55) * mm});
            skLineSegment(sketch, "E132", {"start": v(-1905.3, -254) * mm, "end": v(-1905.3, -236.04) * mm});
            skLineSegment(sketch, "E133", {"start": v(-1987.85, -318.59) * mm, "end": v(-1905.3, -236.04) * mm});
            skLineSegment(sketch, "E134", {"start": v(-1987.85, -318.59) * mm, "end": v(-1987.85, -336.55) * mm});
            skLineSegment(sketch, "E135.bottom", {"start": v(-1892.6, -127) * mm, "end": v(-1803.7, -127) * mm});
            skLineSegment(sketch, "E135.top", {"start": v(-1892.6, -139.7) * mm, "end": v(-1803.7, -139.7) * mm});
            skLineSegment(sketch, "E135.left", {"start": v(-1892.6, -127) * mm, "end": v(-1892.6, -139.7) * mm});
            skLineSegment(sketch, "E135.right", {"start": v(-1803.7, -127) * mm, "end": v(-1803.7, -139.7) * mm});
            skLineSegment(sketch, "E136.bottom", {"start": v(-1892.6, -254) * mm, "end": v(-1803.7, -254) * mm});
            skLineSegment(sketch, "E136.top", {"start": v(-1892.6, -266.7) * mm, "end": v(-1803.7, -266.7) * mm});
            skLineSegment(sketch, "E136.left", {"start": v(-1892.6, -254) * mm, "end": v(-1892.6, -266.7) * mm});
            skLineSegment(sketch, "E136.right", {"start": v(-1803.7, -254) * mm, "end": v(-1803.7, -266.7) * mm});
            skLineSegment(sketch, "E137.bottom", {"start": v(-1892.6, -419.1) * mm, "end": v(-1803.7, -419.1) * mm});
            skLineSegment(sketch, "E137.top", {"start": v(-1892.6, -431.8) * mm, "end": v(-1803.7, -431.8) * mm});
            skLineSegment(sketch, "E137.left", {"start": v(-1892.6, -419.1) * mm, "end": v(-1892.6, -431.8) * mm});
            skLineSegment(sketch, "E137.right", {"start": v(-1803.7, -419.1) * mm, "end": v(-1803.7, -431.8) * mm});
            skLineSegment(sketch, "E138.bottom", {"start": v(-1892.6, -546.1) * mm, "end": v(-1803.7, -546.1) * mm});
            skLineSegment(sketch, "E138.top", {"start": v(-1892.6, -558.8) * mm, "end": v(-1803.7, -558.8) * mm});
            skLineSegment(sketch, "E138.left", {"start": v(-1892.6, -546.1) * mm, "end": v(-1892.6, -558.8) * mm});
            skLineSegment(sketch, "E138.right", {"start": v(-1803.7, -546.1) * mm, "end": v(-1803.7, -558.8) * mm});
            skSolve(sketch);
        }
        {
            var Q0;
            Q0 = qSketchRegion(id + "F44", true);
            extrude(context, id + "F45", {"entities" : qUnion([Q0]), "operationType" : NewBodyOperationType.ADD, "oppositeDirection" : true, "depth" : 25.4 * mm, "offsetDistance" : 25.4 * mm});
        }
    });
